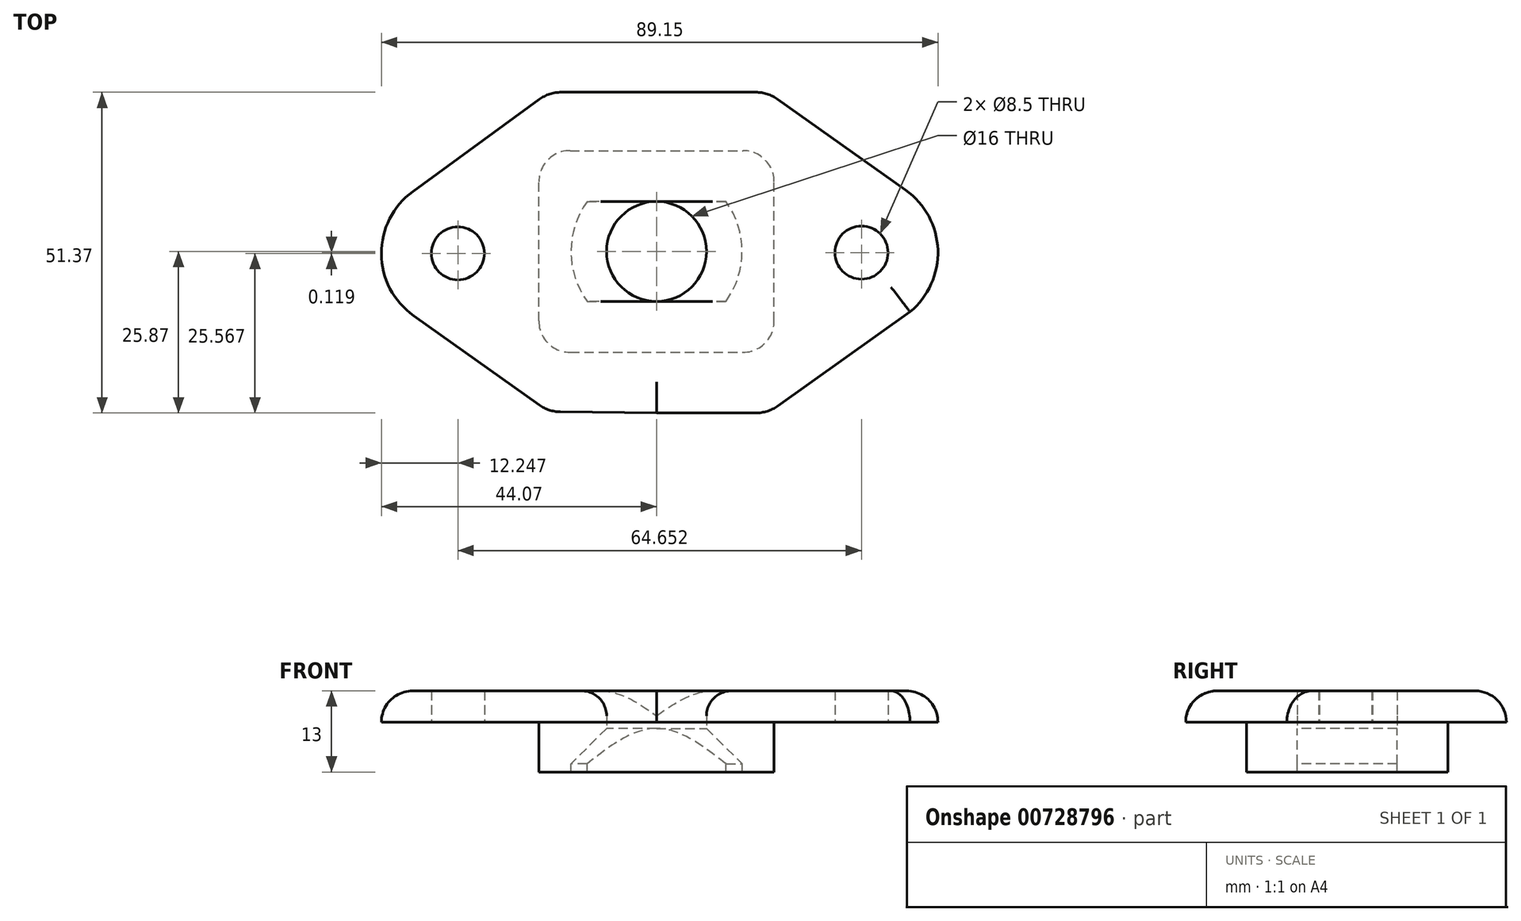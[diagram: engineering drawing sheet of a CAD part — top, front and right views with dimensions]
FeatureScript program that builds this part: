
annotation { "Feature Type Name" : "Feature", "Feature Type Description" : "" }
export const myFeature = defineFeature(function(context is Context, id is Id, definition is map)
    precondition{}
    {
        {
            var Q0;
            Q0=qCreatedBy(makeId("Top.planeOp"),FACE);
            var sketch = newSketch(context, id + "F0", { "sketchPlane" : qUnion([Q0])});
            skCircle(sketch, "E0", {"center": v(-31.82, -0.3) * mm, "radius": 4.25 * mm});
            skCircle(sketch, "E1", {"center": v(32.83, -0.18) * mm, "radius": 4.25 * mm});
            skCircle(sketch, "E2", {"center": v(0, 0) * mm, "radius": 8 * mm});
            skArc(sketch, "E3.0", {"start": v(39.23, -10.63) * mm, "mid": v(45.07, -0.6) * mm, "end": v(39.92, 9.8) * mm});
            skArc(sketch, "E4.0", {"start": v(-39.04, 9.6) * mm, "mid": v(-44.07, -0.38) * mm, "end": v(-38.92, -10.3) * mm});
            skLineSegment(sketch, "E5.0", {"start": v(0, -25.87) * mm, "end": v(15.9, -25.87) * mm});
            skLineSegment(sketch, "E6.0", {"start": v(0, 25.5) * mm, "end": v(-15.25, 25.5) * mm});
            skLineSegment(sketch, "E7.0", {"start": v(0, 25.5) * mm, "end": v(15.9, 25.5) * mm});
            skLineSegment(sketch, "E8.0", {"start": v(0, -25.87) * mm, "end": v(-15.4, -25.68) * mm});
            skLineSegment(sketch, "E9", {"start": v(19.38, 24.4) * mm, "end": v(39.92, 9.8) * mm});
            skLineSegment(sketch, "E10", {"start": v(19.38, -24.76) * mm, "end": v(40.6, -9.66) * mm});
            skLineSegment(sketch, "E11", {"start": v(-18.79, 24.35) * mm, "end": v(-39.04, 9.6) * mm});
            skLineSegment(sketch, "E12", {"start": v(-18.8, -24.58) * mm, "end": v(-38.92, -10.3) * mm});
            skPoint(sketch, "E13.visualSharp", {"position": v(-17.2, 25.5) * mm});
            skArc(sketch, "E13.filletArc", {"start": v(-15.25, 25.5) * mm, "mid": v(-17.11, 25.2) * mm, "end": v(-18.79, 24.35) * mm});
            skPoint(sketch, "E14.visualSharp", {"position": v(17.82, 25.5) * mm});
            skArc(sketch, "E14.filletArc", {"start": v(19.38, 24.4) * mm, "mid": v(17.73, 25.22) * mm, "end": v(15.9, 25.5) * mm});
            skPoint(sketch, "E15.visualSharp", {"position": v(-17.27, -25.66) * mm});
            skArc(sketch, "E15.filletArc", {"start": v(-18.8, -24.58) * mm, "mid": v(-17.18, -25.39) * mm, "end": v(-15.4, -25.68) * mm});
            skPoint(sketch, "E16.visualSharp", {"position": v(17.82, -25.87) * mm});
            skArc(sketch, "E16.filletArc", {"start": v(15.9, -25.87) * mm, "mid": v(17.73, -25.59) * mm, "end": v(19.38, -24.76) * mm});
            skSolve(sketch);
        }
        {
            var Q0;
            Q0=makeQuery(id+"F0.imprint","IMPRINT",FACE,{"disambiguationData":[TD([[makeQuery(id+"F0.imprint","IMPRINT",EDGE,{"derivedFrom":sQuery(id+"F0.wireOp",EDGE,"E0")}),-1.0]])]});
            extrude(context, id + "F1", {"entities" : qUnion([Q0]), "depth" : 5 * mm, "offsetDistance" : 25 * mm});
        }
        {
            var Q0;
            Q0=makeQuery(id+"F1.opExtrude","CAP_EDGE",EDGE,{"disambiguationData":[OSD([sQuery(id+"F0.wireOp",EDGE,"E4.0")])],"isStart":false});
            var Q1;
            Q1=makeQuery(id+"F1.opExtrude","CAP_EDGE",EDGE,{"disambiguationData":[OSD([sQuery(id+"F0.wireOp",EDGE,"E11")])],"isStart":false});
            var Q2;
            Q2=makeQuery(id+"F1.opExtrude","CAP_EDGE",EDGE,{"disambiguationData":[OSD([sQuery(id+"F0.wireOp",EDGE,"E6.0"),sQuery(id+"F0.wireOp",EDGE,"E7.0")])],"isStart":false});
            var Q3;
            Q3=makeQuery(id+"F1.opExtrude","CAP_EDGE",EDGE,{"disambiguationData":[OSD([sQuery(id+"F0.wireOp",EDGE,"E13.filletArc")])],"isStart":false});
            var Q4;
            Q4=makeQuery(id+"F1.opExtrude","CAP_EDGE",EDGE,{"disambiguationData":[OSD([sQuery(id+"F0.wireOp",EDGE,"E14.filletArc")])],"isStart":false});
            var Q5;
            Q5=makeQuery(id+"F1.opExtrude","CAP_EDGE",EDGE,{"disambiguationData":[OSD([sQuery(id+"F0.wireOp",EDGE,"E9")])],"isStart":false});
            var Q6;
            Q6=makeQuery(id+"F1.opExtrude","CAP_EDGE",EDGE,{"disambiguationData":[OSD([sQuery(id+"F0.wireOp",EDGE,"E3.0")])],"isStart":false});
            var Q7;
            Q7=makeQuery(id+"F1.opExtrude","CAP_EDGE",EDGE,{"disambiguationData":[OSD([sQuery(id+"F0.wireOp",EDGE,"E10")])],"isStart":false});
            fillet(context, id + "F2", {"entities" : qUnion([Q0, Q1, Q2, Q3, Q4, Q5, Q6, Q7]), "radius" : 5 * mm, "tangentPropagation" : true, "allowEdgeOverflow" : false});
        }
        {
            var Q0;
            Q0=makeQuery(id+"F1.opExtrude","CAP_FACE",FACE,{"disambiguationData":[OSD([sQuery(id+"F0.wireOp",EDGE,"E0"),sQuery(id+"F0.wireOp",EDGE,"E1"),sQuery(id+"F0.wireOp",EDGE,"E2"),sQuery(id+"F0.wireOp",EDGE,"E3.0"),sQuery(id+"F0.wireOp",EDGE,"E4.0"),sQuery(id+"F0.wireOp",EDGE,"E5.0"),sQuery(id+"F0.wireOp",EDGE,"E6.0"),sQuery(id+"F0.wireOp",EDGE,"E7.0"),sQuery(id+"F0.wireOp",EDGE,"E8.0"),sQuery(id+"F0.wireOp",EDGE,"E9"),sQuery(id+"F0.wireOp",EDGE,"E10"),sQuery(id+"F0.wireOp",EDGE,"E11"),sQuery(id+"F0.wireOp",EDGE,"E12"),sQuery(id+"F0.wireOp",EDGE,"E13.filletArc"),sQuery(id+"F0.wireOp",EDGE,"E14.filletArc"),sQuery(id+"F0.wireOp",EDGE,"E15.filletArc"),sQuery(id+"F0.wireOp",EDGE,"E16.filletArc")])],"isStart":false});
            var sketch = newSketch(context, id + "F3", { "sketchPlane" : qUnion([Q0])});
            skArc(sketch, "E17.0", {"start": v(-11.12, 8) * mm, "mid": v(-13.7, 0) * mm, "end": v(-11.12, -8) * mm});
            skLineSegment(sketch, "E18", {"start": v(-17.22, 0) * mm, "end": v(19.45, 0) * mm, "construction": true});
            skLineSegment(sketch, "E19.0", {"start": v(-11.12, -8) * mm, "end": v(11.12, -8) * mm});
            skLineSegment(sketch, "E20.0", {"start": v(-11.12, 8) * mm, "end": v(11.12, 8) * mm});
            skArc(sketch, "E21.trimOffspring", {"start": v(11.12, -8) * mm, "mid": v(13.7, 0) * mm, "end": v(11.12, 8) * mm});
            skLineSegment(sketch, "E22.0", {"start": v(-13.85, -16.15) * mm, "end": v(13.85, -16.15) * mm});
            skLineSegment(sketch, "E23.0", {"start": v(-13.85, 16.15) * mm, "end": v(13.85, 16.15) * mm});
            skLineSegment(sketch, "E24", {"start": v(0, 36.49) * mm, "end": v(0, -28.36) * mm, "construction": true});
            skLineSegment(sketch, "E25.0", {"start": v(-18.85, 11.15) * mm, "end": v(-18.85, -11.15) * mm});
            skLineSegment(sketch, "E26.0", {"start": v(18.85, 11.15) * mm, "end": v(18.85, -11.15) * mm});
            skArc(sketch, "E27.filletArc", {"start": v(-13.85, 16.15) * mm, "mid": v(-17.39, 14.69) * mm, "end": v(-18.85, 11.15) * mm});
            skArc(sketch, "E28.filletArc", {"start": v(18.85, 11.15) * mm, "mid": v(17.39, 14.69) * mm, "end": v(13.85, 16.15) * mm});
            skArc(sketch, "E29.filletArc", {"start": v(13.85, -16.15) * mm, "mid": v(17.39, -14.69) * mm, "end": v(18.85, -11.15) * mm});
            skArc(sketch, "E30.filletArc", {"start": v(-18.85, -11.15) * mm, "mid": v(-17.39, -14.69) * mm, "end": v(-13.85, -16.15) * mm});
            skSolve(sketch);
        }
        {
            var Q0;
            Q0=makeQuery(id+"F1.opExtrude","CAP_EDGE",EDGE,{"disambiguationData":[OSD([sQuery(id+"F0.wireOp",EDGE,"E2")])],"isStart":false});
            fillet(context, id + "F4", {"entities" : qUnion([Q0]), "radius" : 4 * mm, "tangentPropagation" : true, "allowEdgeOverflow" : false});
        }
        {
            var Q0;
            Q0=makeQuery(id+"F1.opExtrude","CAP_FACE",FACE,{"disambiguationData":[OSD([sQuery(id+"F0.wireOp",EDGE,"E0"),sQuery(id+"F0.wireOp",EDGE,"E1"),sQuery(id+"F0.wireOp",EDGE,"E2"),sQuery(id+"F0.wireOp",EDGE,"E3.0"),sQuery(id+"F0.wireOp",EDGE,"E4.0"),sQuery(id+"F0.wireOp",EDGE,"E5.0"),sQuery(id+"F0.wireOp",EDGE,"E6.0"),sQuery(id+"F0.wireOp",EDGE,"E7.0"),sQuery(id+"F0.wireOp",EDGE,"E8.0"),sQuery(id+"F0.wireOp",EDGE,"E9"),sQuery(id+"F0.wireOp",EDGE,"E10"),sQuery(id+"F0.wireOp",EDGE,"E11"),sQuery(id+"F0.wireOp",EDGE,"E12"),sQuery(id+"F0.wireOp",EDGE,"E13.filletArc"),sQuery(id+"F0.wireOp",EDGE,"E14.filletArc"),sQuery(id+"F0.wireOp",EDGE,"E15.filletArc"),sQuery(id+"F0.wireOp",EDGE,"E16.filletArc")])],"isStart":true});
            var sketch = newSketch(context, id + "F5", { "sketchPlane" : qUnion([Q0])});
            skLineSegment(sketch, "E31.0", {"start": v(-13.86, -16.15) * mm, "end": v(13.84, -16.15) * mm});
            skLineSegment(sketch, "E32.0", {"start": v(-13.86, 16.15) * mm, "end": v(13.84, 16.15) * mm});
            skLineSegment(sketch, "E33.0", {"start": v(18.84, 11.15) * mm, "end": v(18.84, -11.15) * mm});
            skArc(sketch, "E34.filletArc", {"start": v(-13.86, 16.15) * mm, "mid": v(-17.4, 14.69) * mm, "end": v(-18.86, 11.15) * mm});
            skArc(sketch, "E35.filletArc", {"start": v(18.84, 11.15) * mm, "mid": v(17.38, 14.69) * mm, "end": v(13.84, 16.15) * mm});
            skArc(sketch, "E36.filletArc", {"start": v(13.84, -16.15) * mm, "mid": v(17.38, -14.69) * mm, "end": v(18.84, -11.15) * mm});
            skArc(sketch, "E37.filletArc", {"start": v(-18.86, -11.15) * mm, "mid": v(-17.4, -14.69) * mm, "end": v(-13.86, -16.15) * mm});
            skLineSegment(sketch, "E38", {"start": v(-18.86, 11.15) * mm, "end": v(-18.86, -11.15) * mm});
            skCircle(sketch, "E39", {"center": v(0, 0) * mm, "radius": 8 * mm});
            skSolve(sketch);
        }
        {
            var Q0;
            Q0=makeQuery(id+"F5.imprint","IMPRINT",FACE,{"disambiguationData":[TD([[makeQuery(id+"F5.imprint","IMPRINT",EDGE,{"derivedFrom":sQuery(id+"F5.wireOp",EDGE,"E31.0")}),1.0]])]});
            extrude(context, id + "F6", {"entities" : qUnion([Q0]), "operationType" : NewBodyOperationType.ADD, "depth" : 8 * mm, "offsetDistance" : 25 * mm});
        }
        {
            var Q0;
            Q0=makeQuery(id+"F6.opExtrude","CAP_EDGE",EDGE,{"disambiguationData":[OSD([sQuery(id+"F5.wireOp",EDGE,"E39")])],"isStart":false});
            chamfer(context, id + "F7", {"entities" : qUnion([Q0]), "width" : 7 * mm, "tangentPropagation" : true});
        }
        {
            var Q0;
            {var subQ4=sQuery(id+"F3.wireOp",EDGE,"E17.0");Q0=makeQuery(id+"F3.imprint","IMPRINT",FACE,{"disambiguationData":[TD([[makeQuery(id+"F3.imprint","IMPRINT",EDGE,{"derivedFrom":subQ4}),-1.0]])]});}
            var Q1;
            Q1=makeQuery(id+"F6.opExtrude","CAP_FACE",FACE,{"disambiguationData":[OSD([sQuery(id+"F5.wireOp",EDGE,"E31.0"),sQuery(id+"F5.wireOp",EDGE,"E32.0"),sQuery(id+"F5.wireOp",EDGE,"E33.0"),sQuery(id+"F5.wireOp",EDGE,"E34.filletArc"),sQuery(id+"F5.wireOp",EDGE,"E35.filletArc"),sQuery(id+"F5.wireOp",EDGE,"E36.filletArc"),sQuery(id+"F5.wireOp",EDGE,"E37.filletArc"),sQuery(id+"F5.wireOp",EDGE,"E38"),sQuery(id+"F5.wireOp",EDGE,"E39")])],"isStart":false});
            extrude(context, id + "F8", {"entities" : qUnion([Q0]), "operationType" : NewBodyOperationType.ADD, "endBound" : BoundingType.UP_TO_SURFACE, "oppositeDirection" : true, "depth" : 25 * mm, "endBoundEntityFace" : qUnion([Q1]), "offsetDistance" : 25 * mm});
        }
    });
